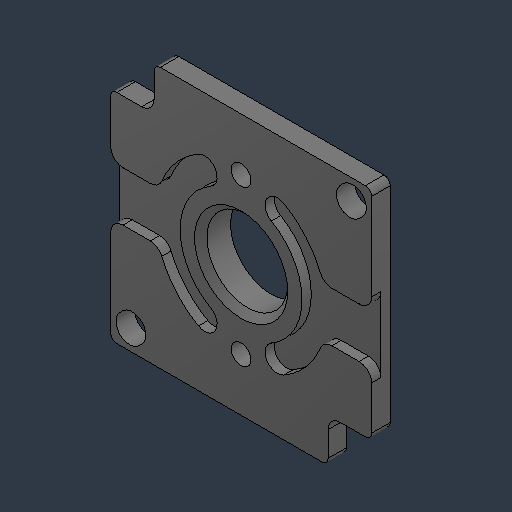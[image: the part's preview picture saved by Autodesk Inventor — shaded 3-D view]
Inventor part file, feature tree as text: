
AUTODESK INVENTOR PART (.ipt)
format: ipt  version: 2024.3 (Build 283343000, 343)  size: 243,712 bytes
history: native  units: in
note: dims shown in document units (in); Inventor stores cm internally (conversion verified against a paired STEP export)
features: fillet x1
ambient origin geometry x8: Origin, YZ Plane, XZ Plane, XY Plane, X Axis, Y Axis, Z Axis, Center Point
bodies: Solid1 (feature_tree)
feature tree (1):
  fillet  "Fillet4"  [1 undecoded]
note: 1 required parameter value undecoded (feature->parameter linkage not recoverable at this tier; creation-order binding heuristic only, values carry confidence <= 0.55)
